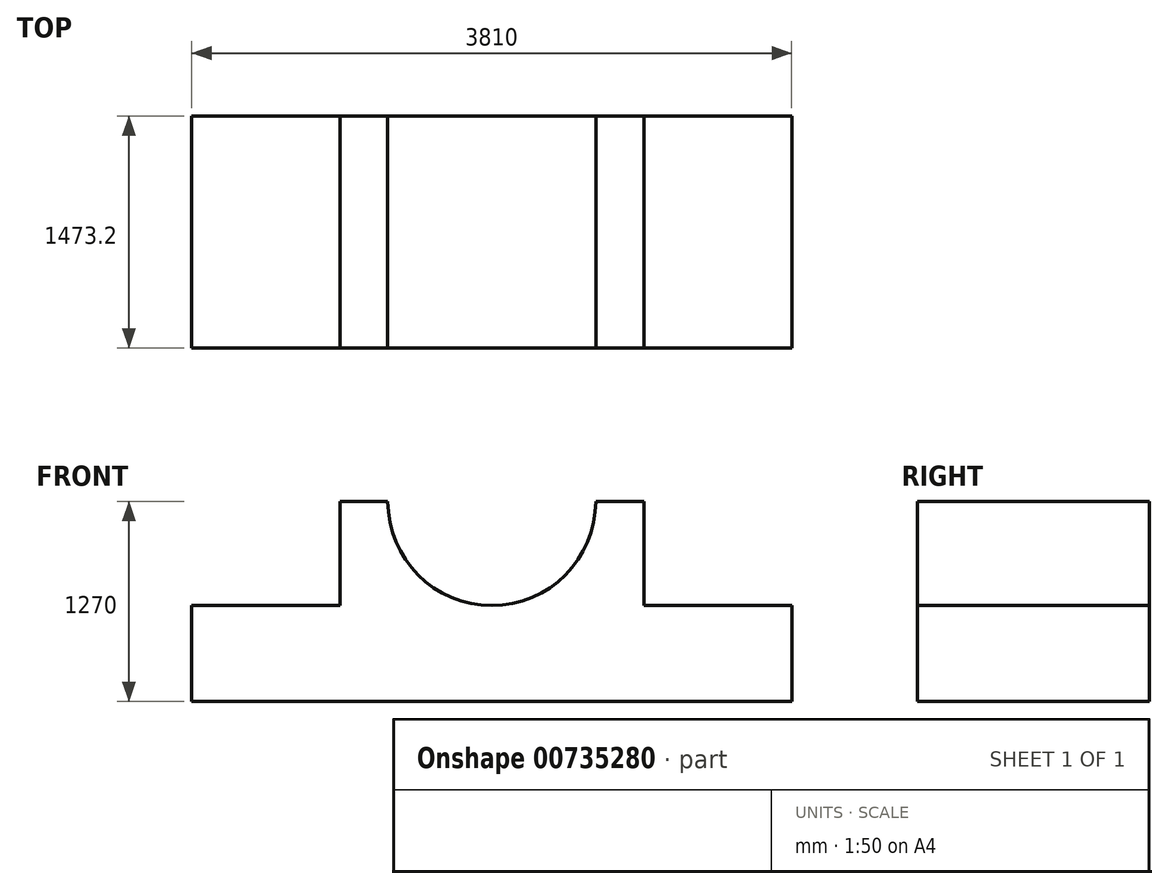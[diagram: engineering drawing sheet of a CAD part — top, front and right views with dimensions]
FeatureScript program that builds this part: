
annotation { "Feature Type Name" : "Feature", "Feature Type Description" : "" }
export const myFeature = defineFeature(function(context is Context, id is Id, definition is map)
    precondition{}
    {
        {
            var Q0;
            Q0=qCreatedBy(makeId("Front.planeOp"),FACE);
            var sketch = newSketch(context, id + "F0", { "sketchPlane" : qUnion([Q0])});
            skLineSegment(sketch, "E0", {"start": v(-693.39, 0) * mm, "end": v(3116.61, 0) * mm});
            skLineSegment(sketch, "E1", {"start": v(3116.61, 0) * mm, "end": v(3116.61, 609.6) * mm});
            skLineSegment(sketch, "E2", {"start": v(-693.39, 0) * mm, "end": v(-693.39, 609.6) * mm});
            skLineSegment(sketch, "E3", {"start": v(-693.39, 609.6) * mm, "end": v(246.41, 609.6) * mm});
            skLineSegment(sketch, "E4", {"start": v(3116.61, 609.6) * mm, "end": v(2176.81, 609.6) * mm});
            skLineSegment(sketch, "E5", {"start": v(2176.81, 609.6) * mm, "end": v(2176.81, 1270) * mm});
            skLineSegment(sketch, "E6", {"start": v(246.41, 609.6) * mm, "end": v(246.41, 1270) * mm});
            skLineSegment(sketch, "E7", {"start": v(246.41, 1270) * mm, "end": v(551.21, 1270) * mm});
            skLineSegment(sketch, "E8", {"start": v(551.21, 1270) * mm, "end": v(1211.61, 1270) * mm});
            skCircle(sketch, "E9", {"center": v(1211.61, 1270) * mm, "radius": 660.4 * mm});
            skLineSegment(sketch, "E10", {"start": v(2176.81, 1270) * mm, "end": v(1872.01, 1270) * mm});
            skSolve(sketch);
        }
        {
            var Q0;
            Q0=makeQuery(id+"F0.imprint","IMPRINT",FACE,{"disambiguationData":[TD([[makeQuery(id+"F0.imprint","IMPRINT",EDGE,{"derivedFrom":sQuery(id+"F0.wireOp",EDGE,"E0")}),1.0]])]});
            extrude(context, id + "F1", {"entities" : qUnion([Q0]), "depth" : 1473.2 * mm, "offsetDistance" : 25.4 * mm});
        }
    });
